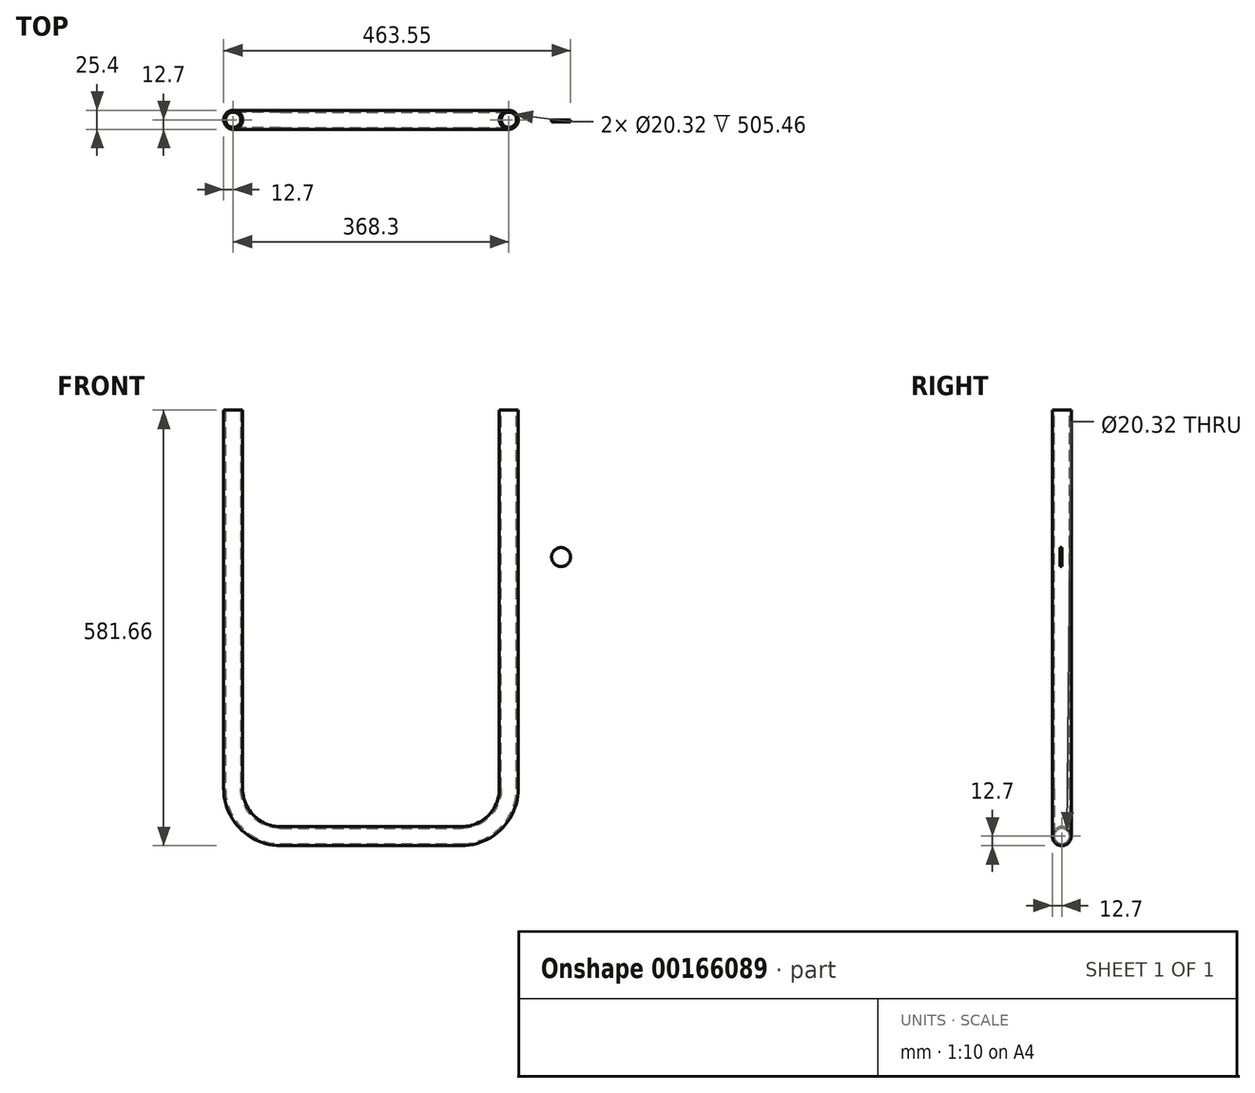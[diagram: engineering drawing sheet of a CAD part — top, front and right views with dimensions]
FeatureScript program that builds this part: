
annotation { "Feature Type Name" : "Feature", "Feature Type Description" : "" }
export const myFeature = defineFeature(function(context is Context, id is Id, definition is map)
    precondition{}
    {
        {
            var Q0;
            Q0=qCreatedBy(makeId("Front.planeOp"),FACE);
            var sketch = newSketch(context, id + "F0", { "sketchPlane" : qUnion([Q0])});
            skPoint(sketch, "E0", {"position": v(-184.15, 0) * mm});
            skPoint(sketch, "E1", {"position": v(184.15, 0) * mm});
            skLineSegment(sketch, "E2", {"start": v(-184.15, 571.5) * mm, "end": v(-184.15, 63.5) * mm});
            skLineSegment(sketch, "E3", {"start": v(184.15, 63.5) * mm, "end": v(184.15, 571.5) * mm});
            skLineSegment(sketch, "E4", {"start": v(-184.15, 571.5) * mm, "end": v(-196.85, 571.5) * mm});
            skLineSegment(sketch, "E5", {"start": v(-120.65, 0) * mm, "end": v(120.65, 0) * mm});
            skArc(sketch, "E6.filletArc", {"start": v(-184.15, 63.5) * mm, "mid": v(-165.55, 18.6) * mm, "end": v(-120.65, 0) * mm});
            skArc(sketch, "E7.filletArc", {"start": v(120.65, 0) * mm, "mid": v(165.55, 18.6) * mm, "end": v(184.15, 63.5) * mm});
            skPoint(sketch, "E8", {"position": v(184.15, 114.3) * mm});
            skPoint(sketch, "E9.MirrorP", {"position": v(-184.15, 114.3) * mm});
            skSolve(sketch);
        }
        {
            var Q0;
            Q0=sQuery(id+"F0.wireOp",EDGE,"E4");
            var Q1;
            Q1=sQuery(id+"F0.wireOp",EDGE,"E2");
            revolve(context, id + "F1", {"bodyType" : ToolBodyType.SURFACE, "surfaceEntities" : qUnion([Q0]), "axis" : qUnion([Q1]), "revolveType" : RevolveType.FULL});
        }
        {
            var Q0;
            Q0=makeQuery(id+"F1.opRevolve","SWEPT_FACE",FACE,{"disambiguationData":[OSD([sQuery(id+"F0.wireOp",EDGE,"E4")])]});
            var Q1;
            Q1=sQuery(id+"F0.wireOp",EDGE,"E2");
            var Q2;
            Q2=sQuery(id+"F0.wireOp",EDGE,"E6.filletArc");
            var Q3;
            Q3=sQuery(id+"F0.wireOp",EDGE,"E5");
            var Q4;
            Q4=sQuery(id+"F0.wireOp",EDGE,"E7.filletArc");
            var Q5;
            Q5=sQuery(id+"F0.wireOp",EDGE,"E3");
            sweep(context, id + "F2", {"profiles" : qUnion([Q0]), "path" : qUnion([Q1, Q2, Q3, Q4, Q5])});
        }
        {
            var Q0;
            Q0=makeQuery(id+"F2.opSweep","SWEPT_FACE",FACE,{"disambiguationData":[OSD([sQuery(id+"F0.wireOp",VERTEX,"E4.end"),sQuery(id+"F0.wireOp",EDGE,"E3")])]});
            var Q1;
            Q1=makeQuery(id+"F2.opSweep","SWEPT_FACE",FACE,{"disambiguationData":[OSD([sQuery(id+"F0.wireOp",VERTEX,"E4.end"),sQuery(id+"F0.wireOp",EDGE,"E7.filletArc")])]});
            var Q2;
            Q2=makeQuery(id+"F2.opSweep","SWEPT_FACE",FACE,{"disambiguationData":[OSD([sQuery(id+"F0.wireOp",VERTEX,"E4.end"),sQuery(id+"F0.wireOp",EDGE,"E5")])]});
            var Q3;
            Q3=makeQuery(id+"F2.opSweep","SWEPT_FACE",FACE,{"disambiguationData":[OSD([sQuery(id+"F0.wireOp",VERTEX,"E4.end"),sQuery(id+"F0.wireOp",EDGE,"E6.filletArc")])]});
            var Q4;
            Q4=makeQuery(id+"F2.opSweep","SWEPT_FACE",FACE,{"disambiguationData":[OSD([sQuery(id+"F0.wireOp",VERTEX,"E4.end"),sQuery(id+"F0.wireOp",EDGE,"E2")])]});
            var Q5;
            Q5=makeQuery(id+"F2.opSweep","SWEPT_BODY",BODY,{"disambiguationData":[OSD([sQuery(id+"F0.wireOp",EDGE,"E3"),sQuery(id+"F0.wireOp",EDGE,"E4")])]});
            shell(context, id + "F3", {"isHollow" : true, "entities" : qUnion([Q0, Q1, Q2, Q3, Q4]), "parts" : qUnion([Q5]), "thickness" : 2.54 * mm});
        }
        {
            var Q0;
            Q0=makeQuery(id+"F1.opRevolve","SWEPT_BODY",BODY,{"disambiguationData":[OSD([sQuery(id+"F0.wireOp",EDGE,"E4")])]});
            deleteBodies(context, id + "F4", {"entities" : qUnion([Q0])});
        }
        {
            var Q0;
            Q0=makeQuery(id+"F2.opSweep","CAP_FACE",FACE,{"disambiguationData":[OSD([sQuery(id+"F0.wireOp",VERTEX,"E2.start"),sQuery(id+"F0.wireOp",EDGE,"E4")])],"isStart":true});
            var Q1;
            Q1=makeQuery(id+"F2.opSweep","CAP_FACE",FACE,{"disambiguationData":[OSD([sQuery(id+"F0.wireOp",VERTEX,"E3.end"),sQuery(id+"F0.wireOp",EDGE,"E4")])],"isStart":false});
            extrude(context, id + "F5", {"entities" : qUnion([Q0, Q1]), "operationType" : NewBodyOperationType.REMOVE, "oppositeDirection" : true, "depth" : 2.54 * mm});
        }
        {
            var Q0;
            Q0=qCreatedBy(makeId("Front.planeOp"),FACE);
            var sketch = newSketch(context, id + "F6", { "sketchPlane" : qUnion([Q0])});
            skCircle(sketch, "E10", {"center": v(254, 372.74) * mm, "radius": 12.7 * mm});
            skCircle(sketch, "E11.MirrorC", {"center": v(-254, 372.74) * mm, "radius": 12.7 * mm});
            skSolve(sketch);
        }
        {
            var Q0;
            Q0=makeQuery(id+"F6.imprint","IMPRINT",FACE,{"disambiguationData":[TD([[makeQuery(id+"F6.imprint","IMPRINT",EDGE,{"derivedFrom":sQuery(id+"F6.wireOp",EDGE,"E10")}),1.0]])]});
            var Q1;
            Q1=makeQuery(id+"F6.imprint","IMPRINT",FACE,{"disambiguationData":[TD([[makeQuery(id+"F6.imprint","IMPRINT",EDGE,{"derivedFrom":sQuery(id+"F6.wireOp",EDGE,"E11.MirrorC")}),-1.0]])]});
            extrude(context, id + "F7", {"entities" : qUnion([Q0, Q1]), "depth" : 2.54 * mm});
        }
    });
